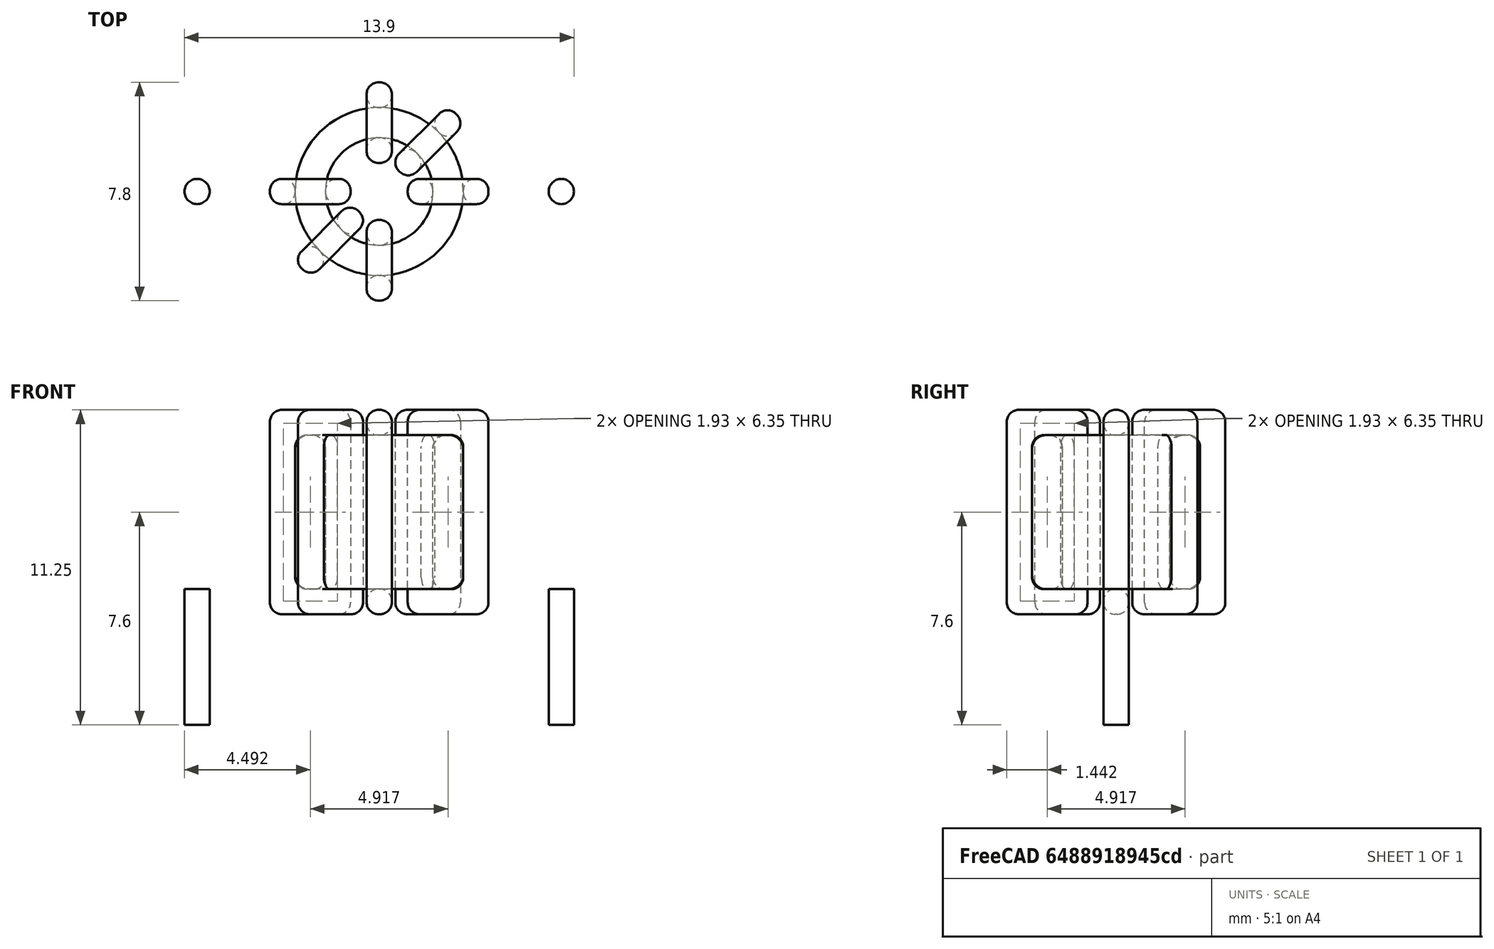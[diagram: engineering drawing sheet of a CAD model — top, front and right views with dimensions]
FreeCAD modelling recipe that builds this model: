
FCSTD DOCUMENT  (FreeCAD 0.16R6703 (Git))
Label: L_Toroid_Horizontal_D7.8mm_P13.00mm_Diameter9-5mm_Amidon-T30
License: All rights reserved
LicenseURL: http://en.wikipedia.org/wiki/All_rights_reserved
objects: Sketcher::SketchObject×6, PartDesign::Pad×6, PartDesign::Fillet×5, Spreadsheet::Sheet×1
note: 23 computed .brp shape members not serialized (recipe doc carries the construction recipe); baked Part::Feature solids carry a one-line shape summary decoded from their .brp

FEATURE [Spreadsheet::Sheet] Spreadsheet  label="dimensions"
  cells = A1=Wx; B1(Wx)=7.7978; C1(WW)=3.8354; D1=7.7978; A2=Wy; B2(Wy)=7.7978; D2=7.7978; A3=RM; B3(RMx)=13; C3(RMy)=0; A4=d_wire; B4(d_wire)=0.8999999999999999; A5=H; B5(H)=5.5; A6=offsetx; B6(offsetx)=-2.6011
FEATURE [Sketcher::SketchObject] Sketch
  Placement = pos=(0,0,1.4) rot=(0,0,1;0rad)
  expr: Placement.Base.z = 0.5 + Spreadsheet.d_wire
  expr: Constraints[0] = Spreadsheet.Wx / 2 - Spreadsheet.d_wire
  expr: Constraints[4] = Spreadsheet.WW / 2
  expr: Constraints[2] = Spreadsheet.RMy / 2
  expr: Constraints[1] = Spreadsheet.RMx / 2
  sketch-geometry (2):
    g0: Circle CenterX=6.5 CenterY=0 CenterZ=0 NormalX=0 NormalY=0 NormalZ=1 Radius=2.9989
    g1: Circle CenterX=6.5 CenterY=0 CenterZ=0 NormalX=0 NormalY=0 NormalZ=1 Radius=1.9177
  constraints (5):
    c: Radius(g0) = 2.9989
    c: DistanceX(g-1,g0) = 6.5
    c: DistanceY(g-1,g0) = 0
    c: Coincident(g1,g0)
    c: Radius(g1) = 1.9177
FEATURE [PartDesign::Pad] Pad
  Length = 5.5
  Length2 = 100
  Placement = pos=(0,0,1.4) rot=(0,0,1;0rad)
  Sketch = -> Sketch
  Type = 0
  expr: Length = Spreadsheet.H
FEATURE [Sketcher::SketchObject] Sketch001
  Placement = pos=(0,0,0.95) rot=(0,0,1;0rad)
  expr: Placement.Base.z = 0.5 + Spreadsheet.d_wire * 0.5
  expr: Constraints[4] = Spreadsheet.RMx
  expr: Constraints[2] = Spreadsheet.RMy
  expr: Constraints[1] = Spreadsheet.d_wire / 2
  sketch-geometry (2):
    g0: Circle CenterX=0 CenterY=0 CenterZ=0 NormalX=0 NormalY=0 NormalZ=1 Radius=0.45
    g1: Circle CenterX=13 CenterY=0 CenterZ=0 NormalX=0 NormalY=0 NormalZ=1 Radius=0.45
  constraints (5):
    c: Equal(g0,g1)
    c: Radius(g0) = 0.45
    c: DistanceY(g-1,g1) = 0
    c: Coincident(g0,g-1)
    c: DistanceX(g-1,g1) = 13
FEATURE [PartDesign::Pad] Pad001
  Length = 0.45
  Length2 = 4.4
  Placement = pos=(0,0,0.95) rot=(0,0,1;0rad)
  Reversed = true
  Sketch = -> Sketch001
  Type = 4
  expr: Length2 = 3.5 + Spreadsheet.d_wire
  expr: Length = Spreadsheet.d_wire / 2
FEATURE [PartDesign::Fillet] Fillet
  Base = -> Pad [Edge6,Edge3,Edge2]
  Placement = pos=(0,0,1.4) rot=(0,0,1;0rad)
  Radius = 0.5
FEATURE [Sketcher::SketchObject] Sketch003
  Placement = pos=(6.5,0,0) rot=(1,0,0;1.5708rad)
  expr: Placement.Base.x = Spreadsheet.RMx / 2
  expr: Constraints[49] = Spreadsheet.Wx - Spreadsheet.d_wire * 2
  expr: Constraints[44] = Spreadsheet.d_wire
  expr: Constraints[23] = Spreadsheet.H
  expr: Constraints[22] = Spreadsheet.Wx / 2 - Spreadsheet.d_wire
  expr: Placement.Base.y = Spreadsheet.RMy / 2
  expr: Constraints[21] = (Spreadsheet.Wx - Spreadsheet.WW) / 2 - Spreadsheet.d_wire
  expr: Constraints[19] = Spreadsheet.d_wire
  expr: Constraints[17] = Spreadsheet.d_wire
  expr: Constraints[18] = Spreadsheet.d_wire
  expr: Constraints[16] = Spreadsheet.d_wire
  sketch-geometry (16):
    g0: LineSegment StartX=-1.0177 StartY=0.5 StartZ=0 EndX=-3.8989 EndY=0.5 EndZ=0
    g1: LineSegment StartX=-3.8989 StartY=0.5 StartZ=0 EndX=-3.8989 EndY=7.8 EndZ=0
    g2: LineSegment StartX=-3.8989 StartY=7.8 StartZ=0 EndX=-1.0177 EndY=7.8 EndZ=0
    g3: LineSegment StartX=-1.0177 StartY=7.8 StartZ=0 EndX=-1.0177 EndY=0.5 EndZ=0
    g4: LineSegment StartX=-2.9989 StartY=6.9 StartZ=0 EndX=-1.9177 EndY=6.9 EndZ=0
    g5: LineSegment StartX=-1.9177 StartY=6.9 StartZ=0 EndX=-1.9177 EndY=1.4 EndZ=0
    g6: LineSegment StartX=-1.9177 StartY=1.4 StartZ=0 EndX=-2.9989 EndY=1.4 EndZ=0
    g7: LineSegment StartX=-2.9989 StartY=1.4 StartZ=0 EndX=-2.9989 EndY=6.9 EndZ=0
    g8: LineSegment StartX=1.0177 StartY=7.8 StartZ=0 EndX=3.8989 EndY=7.8 EndZ=0
    g9: LineSegment StartX=3.8989 StartY=7.8 StartZ=0 EndX=3.8989 EndY=0.5 EndZ=0
    g10: LineSegment StartX=3.8989 StartY=0.5 StartZ=0 EndX=1.0177 EndY=0.5 EndZ=0
    g11: LineSegment StartX=1.0177 StartY=0.5 StartZ=0 EndX=1.0177 EndY=7.8 EndZ=0
    g12: LineSegment StartX=1.9177 StartY=6.9 StartZ=0 EndX=2.9989 EndY=6.9 EndZ=0
    g13: LineSegment StartX=2.9989 StartY=6.9 StartZ=0 EndX=2.9989 EndY=1.4 EndZ=0
    g14: LineSegment StartX=2.9989 StartY=1.4 StartZ=0 EndX=1.9177 EndY=1.4 EndZ=0
    g15: LineSegment StartX=1.9177 StartY=1.4 StartZ=0 EndX=1.9177 EndY=6.9 EndZ=0
  constraints (50):
    c: Horizontal(g0)
    c: Coincident(g1,g0)
    c: Vertical(g1)
    c: Coincident(g2,g1)
    c: Horizontal(g2)
    c: Coincident(g3,g2)
    c: Coincident(g3,g0)
    c: Vertical(g3)
    c: Coincident(g4,g5)
    c: Coincident(g5,g6)
    c: Coincident(g6,g7)
    c: Coincident(g7,g4)
    c: Horizontal(g4)
    c: Horizontal(g6)
    c: Vertical(g5)
    c: Vertical(g7)
    c: DistanceX(g1,g4) = 0.9
    c: DistanceY(g4,g1) = 0.9
    c: DistanceX(g5,g0) = 0.9
    c: DistanceY(g0,g5) = 0.9
    c: DistanceY(g-1,g0) = 0.5
    c: DistanceX(g6,g6) = 1.0812
    c: DistanceX(g6,g-1) = 2.9989
    c: DistanceY(g7,g7) = 5.5
    c: Coincident(g8,g9)
    c: Coincident(g9,g10)
    c: Coincident(g10,g11)
    c: Coincident(g11,g8)
    c: Horizontal(g8)
    c: Horizontal(g10)
    c: Vertical(g9)
    c: Vertical(g11)
    c: Coincident(g12,g13)
    c: Coincident(g13,g14)
    c: Coincident(g14,g15)
    c: Coincident(g15,g12)
    c: Horizontal(g12)
    c: Horizontal(g14)
    c: Vertical(g13)
    c: Vertical(g15)
    c: DistanceY(g8,g2) = 0
    c: DistanceY(g10,g0) = 0
    c: DistanceY(g14,g5) = 0
    c: DistanceY(g12,g4) = 0
    c: DistanceX(g8,g12) = 0.9
    c: Equal(g8,g2)
    c: Equal(g12,g4)
    c: Equal(g9,g1)
    c: Equal(g13,g7)
    c: DistanceX(g4,g12) = 5.9978
FEATURE [PartDesign::Pad] Pad002
  Length = 0.9
  Length2 = 100
  Midplane = true
  Placement = pos=(6.5,0,0) rot=(1,0,0;1.5708rad)
  Sketch = -> Sketch003
  Type = 0
  expr: Length = Spreadsheet.d_wire
FEATURE [PartDesign::Fillet] Fillet001
  Base = -> Pad002 [Edge38,Edge41,Edge42,Edge43,Edge29,Edge32,Edge33,Edge34,Edge25,Edge35,Edge36,Edge13,Edge14,Edge15,Edge16,Edge17,Edge18,Edge19,Edge1,Edge2,Edge3,Edge4,Edge5,Edge6,Edge7,Edge37,Edge39,Edge40,Edge20,Edge23,Edge24,Edge21,Edge22,Edge8,Edge9,Edge10,Edge11,Edge12,Edge26,Edge27,+8 more]
  Placement = pos=(6.5,0,0) rot=(1,0,0;1.5708rad)
  Radius = 0.423
  expr: Radius = Spreadsheet.d_wire * 0.47
FEATURE [Sketcher::SketchObject] Sketch004
  Placement = pos=(6.5,0,0) rot=(0.862856,0.357407,0.357407;1.71777rad)
  expr: Placement.Base.x = Spreadsheet.RMx / 2
  expr: Constraints[49] = Spreadsheet.Wx - 2 * Spreadsheet.d_wire
  expr: Constraints[44] = Spreadsheet.d_wire
  expr: Constraints[23] = Spreadsheet.H
  expr: Constraints[22] = Spreadsheet.Wx / 2 - Spreadsheet.d_wire
  expr: Placement.Base.y = Spreadsheet.RMy / 2
  expr: Constraints[21] = (Spreadsheet.Wx - Spreadsheet.WW) / 2 - Spreadsheet.d_wire
  expr: Constraints[19] = Spreadsheet.d_wire
  expr: Constraints[17] = Spreadsheet.d_wire
  expr: Constraints[18] = Spreadsheet.d_wire
  expr: Constraints[16] = Spreadsheet.d_wire
  sketch-geometry (16):
    g0: LineSegment StartX=-1.0177 StartY=0.5 StartZ=0 EndX=-3.8989 EndY=0.5 EndZ=0
    g1: LineSegment StartX=-3.8989 StartY=0.5 StartZ=0 EndX=-3.8989 EndY=7.8 EndZ=0
    g2: LineSegment StartX=-3.8989 StartY=7.8 StartZ=0 EndX=-1.0177 EndY=7.8 EndZ=0
    g3: LineSegment StartX=-1.0177 StartY=7.8 StartZ=0 EndX=-1.0177 EndY=0.5 EndZ=0
    g4: LineSegment StartX=-2.9989 StartY=6.9 StartZ=0 EndX=-1.9177 EndY=6.9 EndZ=0
    g5: LineSegment StartX=-1.9177 StartY=6.9 StartZ=0 EndX=-1.9177 EndY=1.4 EndZ=0
    g6: LineSegment StartX=-1.9177 StartY=1.4 StartZ=0 EndX=-2.9989 EndY=1.4 EndZ=0
    g7: LineSegment StartX=-2.9989 StartY=1.4 StartZ=0 EndX=-2.9989 EndY=6.9 EndZ=0
    g8: LineSegment StartX=1.0177 StartY=7.8 StartZ=0 EndX=3.8989 EndY=7.8 EndZ=0
    g9: LineSegment StartX=3.8989 StartY=7.8 StartZ=0 EndX=3.8989 EndY=0.5 EndZ=0
    g10: LineSegment StartX=3.8989 StartY=0.5 StartZ=0 EndX=1.0177 EndY=0.5 EndZ=0
    g11: LineSegment StartX=1.0177 StartY=0.5 StartZ=0 EndX=1.0177 EndY=7.8 EndZ=0
    g12: LineSegment StartX=1.9177 StartY=6.9 StartZ=0 EndX=2.9989 EndY=6.9 EndZ=0
    g13: LineSegment StartX=2.9989 StartY=6.9 StartZ=0 EndX=2.9989 EndY=1.4 EndZ=0
    g14: LineSegment StartX=2.9989 StartY=1.4 StartZ=0 EndX=1.9177 EndY=1.4 EndZ=0
    g15: LineSegment StartX=1.9177 StartY=1.4 StartZ=0 EndX=1.9177 EndY=6.9 EndZ=0
  constraints (50):
    c: Horizontal(g0)
    c: Coincident(g1,g0)
    c: Vertical(g1)
    c: Coincident(g2,g1)
    c: Horizontal(g2)
    c: Coincident(g3,g2)
    c: Coincident(g3,g0)
    c: Vertical(g3)
    c: Coincident(g4,g5)
    c: Coincident(g5,g6)
    c: Coincident(g6,g7)
    c: Coincident(g7,g4)
    c: Horizontal(g4)
    c: Horizontal(g6)
    c: Vertical(g5)
    c: Vertical(g7)
    c: DistanceX(g1,g4) = 0.9
    c: DistanceY(g4,g1) = 0.9
    c: DistanceX(g5,g0) = 0.9
    c: DistanceY(g0,g5) = 0.9
    c: DistanceY(g-1,g0) = 0.5
    c: DistanceX(g6,g6) = 1.0812
    c: DistanceX(g6,g-1) = 2.9989
    c: DistanceY(g7,g7) = 5.5
    c: Coincident(g8,g9)
    c: Coincident(g9,g10)
    c: Coincident(g10,g11)
    c: Coincident(g11,g8)
    c: Horizontal(g8)
    c: Horizontal(g10)
    c: Vertical(g9)
    c: Vertical(g11)
    c: Coincident(g12,g13)
    c: Coincident(g13,g14)
    c: Coincident(g14,g15)
    c: Coincident(g15,g12)
    c: Horizontal(g12)
    c: Horizontal(g14)
    c: Vertical(g13)
    c: Vertical(g15)
    c: DistanceY(g8,g2) = 0
    c: DistanceY(g10,g0) = 0
    c: DistanceY(g14,g5) = 0
    c: DistanceY(g12,g4) = 0
    c: DistanceX(g8,g12) = 0.9
    c: Equal(g8,g2)
    c: Equal(g12,g4)
    c: Equal(g9,g1)
    c: Equal(g13,g7)
    c: DistanceX(g4,g12) = 5.9978
FEATURE [PartDesign::Pad] Pad003
  Length = 0.9
  Length2 = 100
  Midplane = true
  Placement = pos=(6.5,0,0) rot=(0.862856,0.357407,0.357407;1.71777rad)
  Sketch = -> Sketch004
  Type = 0
  expr: Length = Spreadsheet.d_wire
FEATURE [PartDesign::Fillet] Fillet002
  Base = -> Pad003 [Edge38,Edge41,Edge42,Edge43,Edge29,Edge32,Edge33,Edge34,Edge25,Edge35,Edge36,Edge13,Edge14,Edge15,Edge16,Edge17,Edge18,Edge19,Edge1,Edge2,Edge3,Edge4,Edge5,Edge6,Edge7,Edge37,Edge39,Edge40,Edge20,Edge23,Edge24,Edge21,Edge22,Edge8,Edge9,Edge10,Edge11,Edge12,Edge26,Edge27,+8 more]
  Placement = pos=(6.5,0,0) rot=(0.862856,0.357407,0.357407;1.71777rad)
  Radius = 0.423
  expr: Radius = Spreadsheet.d_wire * 0.47
FEATURE [Sketcher::SketchObject] Sketch005
  Placement = pos=(6.5,0,0) rot=(0.862856,-0.357407,-0.357407;1.71777rad)
  expr: Placement.Base.x = Spreadsheet.RMx / 2
  expr: Constraints[49] = Spreadsheet.Wx - 2 * Spreadsheet.d_wire
  expr: Constraints[44] = Spreadsheet.d_wire
  expr: Constraints[23] = Spreadsheet.H
  expr: Constraints[22] = Spreadsheet.Wx / 2 - Spreadsheet.d_wire
  expr: Placement.Base.y = Spreadsheet.RMy / 2
  expr: Constraints[21] = (Spreadsheet.Wx - Spreadsheet.WW) / 2 - Spreadsheet.d_wire
  expr: Constraints[19] = Spreadsheet.d_wire
  expr: Constraints[17] = Spreadsheet.d_wire
  expr: Constraints[18] = Spreadsheet.d_wire
  expr: Constraints[16] = Spreadsheet.d_wire
  sketch-geometry (16):
    g0: LineSegment StartX=-1.0177 StartY=0.5 StartZ=0 EndX=-3.8989 EndY=0.5 EndZ=0
    g1: LineSegment StartX=-3.8989 StartY=0.5 StartZ=0 EndX=-3.8989 EndY=7.8 EndZ=0
    g2: LineSegment StartX=-3.8989 StartY=7.8 StartZ=0 EndX=-1.0177 EndY=7.8 EndZ=0
    g3: LineSegment StartX=-1.0177 StartY=7.8 StartZ=0 EndX=-1.0177 EndY=0.5 EndZ=0
    g4: LineSegment StartX=-2.9989 StartY=6.9 StartZ=0 EndX=-1.9177 EndY=6.9 EndZ=0
    g5: LineSegment StartX=-1.9177 StartY=6.9 StartZ=0 EndX=-1.9177 EndY=1.4 EndZ=0
    g6: LineSegment StartX=-1.9177 StartY=1.4 StartZ=0 EndX=-2.9989 EndY=1.4 EndZ=0
    g7: LineSegment StartX=-2.9989 StartY=1.4 StartZ=0 EndX=-2.9989 EndY=6.9 EndZ=0
    g8: LineSegment StartX=1.0177 StartY=7.8 StartZ=0 EndX=3.8989 EndY=7.8 EndZ=0
    g9: LineSegment StartX=3.8989 StartY=7.8 StartZ=0 EndX=3.8989 EndY=0.5 EndZ=0
    g10: LineSegment StartX=3.8989 StartY=0.5 StartZ=0 EndX=1.0177 EndY=0.5 EndZ=0
    g11: LineSegment StartX=1.0177 StartY=0.5 StartZ=0 EndX=1.0177 EndY=7.8 EndZ=0
    g12: LineSegment StartX=1.9177 StartY=6.9 StartZ=0 EndX=2.9989 EndY=6.9 EndZ=0
    g13: LineSegment StartX=2.9989 StartY=6.9 StartZ=0 EndX=2.9989 EndY=1.4 EndZ=0
    g14: LineSegment StartX=2.9989 StartY=1.4 StartZ=0 EndX=1.9177 EndY=1.4 EndZ=0
    g15: LineSegment StartX=1.9177 StartY=1.4 StartZ=0 EndX=1.9177 EndY=6.9 EndZ=0
  constraints (50):
    c: Horizontal(g0)
    c: Coincident(g1,g0)
    c: Vertical(g1)
    c: Coincident(g2,g1)
    c: Horizontal(g2)
    c: Coincident(g3,g2)
    c: Coincident(g3,g0)
    c: Vertical(g3)
    c: Coincident(g4,g5)
    c: Coincident(g5,g6)
    c: Coincident(g6,g7)
    c: Coincident(g7,g4)
    c: Horizontal(g4)
    c: Horizontal(g6)
    c: Vertical(g5)
    c: Vertical(g7)
    c: DistanceX(g1,g4) = 0.9
    c: DistanceY(g4,g1) = 0.9
    c: DistanceX(g5,g0) = 0.9
    c: DistanceY(g0,g5) = 0.9
    c: DistanceY(g-1,g0) = 0.5
    c: DistanceX(g6,g6) = 1.0812
    c: DistanceX(g6,g-1) = 2.9989
    c: DistanceY(g7,g7) = 5.5
    c: Coincident(g8,g9)
    c: Coincident(g9,g10)
    c: Coincident(g10,g11)
    c: Coincident(g11,g8)
    c: Horizontal(g8)
    c: Horizontal(g10)
    c: Vertical(g9)
    c: Vertical(g11)
    c: Coincident(g12,g13)
    c: Coincident(g13,g14)
    c: Coincident(g14,g15)
    c: Coincident(g15,g12)
    c: Horizontal(g12)
    c: Horizontal(g14)
    c: Vertical(g13)
    c: Vertical(g15)
    c: DistanceY(g8,g2) = 0
    c: DistanceY(g10,g0) = 0
    c: DistanceY(g14,g5) = 0
    c: DistanceY(g12,g4) = 0
    c: DistanceX(g8,g12) = 0.9
    c: Equal(g8,g2)
    c: Equal(g12,g4)
    c: Equal(g9,g1)
    c: Equal(g13,g7)
    c: DistanceX(g4,g12) = 5.9978
FEATURE [PartDesign::Pad] Pad004
  Length = 0.9
  Length2 = 100
  Midplane = true
  Placement = pos=(6.5,0,0) rot=(0.862856,-0.357407,-0.357407;1.71777rad)
  Sketch = -> Sketch005
  Type = 0
  expr: Length = Spreadsheet.d_wire
FEATURE [PartDesign::Fillet] Fillet003
  Base = -> Pad004 [Edge38,Edge41,Edge42,Edge43,Edge29,Edge32,Edge33,Edge34,Edge25,Edge35,Edge36,Edge13,Edge14,Edge15,Edge16,Edge17,Edge18,Edge19,Edge1,Edge2,Edge3,Edge4,Edge5,Edge6,Edge7,Edge37,Edge39,Edge40,Edge20,Edge23,Edge24,Edge21,Edge22,Edge8,Edge9,Edge10,Edge11,Edge12,Edge26,Edge27,+8 more]
  Placement = pos=(6.5,0,0) rot=(0.862856,-0.357407,-0.357407;1.71777rad)
  Radius = 0.423
  expr: Radius = Spreadsheet.d_wire * 0.47
FEATURE [Sketcher::SketchObject] Sketch006
  Placement = pos=(6.5,0,0) rot=(0.57735,0.57735,0.57735;2.0944rad)
  expr: Placement.Base.x = Spreadsheet.RMx / 2
  expr: Constraints[49] = Spreadsheet.Wx - Spreadsheet.d_wire * 2
  expr: Constraints[44] = Spreadsheet.d_wire
  expr: Constraints[23] = Spreadsheet.H
  expr: Constraints[22] = Spreadsheet.Wx / 2 - Spreadsheet.d_wire
  expr: Placement.Base.y = Spreadsheet.RMy / 2
  expr: Constraints[21] = (Spreadsheet.Wx - Spreadsheet.WW) / 2 - Spreadsheet.d_wire
  expr: Constraints[19] = Spreadsheet.d_wire
  expr: Constraints[17] = Spreadsheet.d_wire
  expr: Constraints[18] = Spreadsheet.d_wire
  expr: Constraints[16] = Spreadsheet.d_wire
  sketch-geometry (16):
    g0: LineSegment StartX=-1.0177 StartY=0.5 StartZ=0 EndX=-3.8989 EndY=0.5 EndZ=0
    g1: LineSegment StartX=-3.8989 StartY=0.5 StartZ=0 EndX=-3.8989 EndY=7.8 EndZ=0
    g2: LineSegment StartX=-3.8989 StartY=7.8 StartZ=0 EndX=-1.0177 EndY=7.8 EndZ=0
    g3: LineSegment StartX=-1.0177 StartY=7.8 StartZ=0 EndX=-1.0177 EndY=0.5 EndZ=0
    g4: LineSegment StartX=-2.9989 StartY=6.9 StartZ=0 EndX=-1.9177 EndY=6.9 EndZ=0
    g5: LineSegment StartX=-1.9177 StartY=6.9 StartZ=0 EndX=-1.9177 EndY=1.4 EndZ=0
    g6: LineSegment StartX=-1.9177 StartY=1.4 StartZ=0 EndX=-2.9989 EndY=1.4 EndZ=0
    g7: LineSegment StartX=-2.9989 StartY=1.4 StartZ=0 EndX=-2.9989 EndY=6.9 EndZ=0
    g8: LineSegment StartX=1.0177 StartY=7.8 StartZ=0 EndX=3.8989 EndY=7.8 EndZ=0
    g9: LineSegment StartX=3.8989 StartY=7.8 StartZ=0 EndX=3.8989 EndY=0.5 EndZ=0
    g10: LineSegment StartX=3.8989 StartY=0.5 StartZ=0 EndX=1.0177 EndY=0.5 EndZ=0
    g11: LineSegment StartX=1.0177 StartY=0.5 StartZ=0 EndX=1.0177 EndY=7.8 EndZ=0
    g12: LineSegment StartX=1.9177 StartY=6.9 StartZ=0 EndX=2.9989 EndY=6.9 EndZ=0
    g13: LineSegment StartX=2.9989 StartY=6.9 StartZ=0 EndX=2.9989 EndY=1.4 EndZ=0
    g14: LineSegment StartX=2.9989 StartY=1.4 StartZ=0 EndX=1.9177 EndY=1.4 EndZ=0
    g15: LineSegment StartX=1.9177 StartY=1.4 StartZ=0 EndX=1.9177 EndY=6.9 EndZ=0
  constraints (50):
    c: Horizontal(g0)
    c: Coincident(g1,g0)
    c: Vertical(g1)
    c: Coincident(g2,g1)
    c: Horizontal(g2)
    c: Coincident(g3,g2)
    c: Coincident(g3,g0)
    c: Vertical(g3)
    c: Coincident(g4,g5)
    c: Coincident(g5,g6)
    c: Coincident(g6,g7)
    c: Coincident(g7,g4)
    c: Horizontal(g4)
    c: Horizontal(g6)
    c: Vertical(g5)
    c: Vertical(g7)
    c: DistanceX(g1,g4) = 0.9
    c: DistanceY(g4,g1) = 0.9
    c: DistanceX(g5,g0) = 0.9
    c: DistanceY(g0,g5) = 0.9
    c: DistanceY(g-1,g0) = 0.5
    c: DistanceX(g6,g6) = 1.0812
    c: DistanceX(g6,g-1) = 2.9989
    c: DistanceY(g7,g7) = 5.5
    c: Coincident(g8,g9)
    c: Coincident(g9,g10)
    c: Coincident(g10,g11)
    c: Coincident(g11,g8)
    c: Horizontal(g8)
    c: Horizontal(g10)
    c: Vertical(g9)
    c: Vertical(g11)
    c: Coincident(g12,g13)
    c: Coincident(g13,g14)
    c: Coincident(g14,g15)
    c: Coincident(g15,g12)
    c: Horizontal(g12)
    c: Horizontal(g14)
    c: Vertical(g13)
    c: Vertical(g15)
    c: DistanceY(g8,g2) = 0
    c: DistanceY(g10,g0) = 0
    c: DistanceY(g14,g5) = 0
    c: DistanceY(g12,g4) = 0
    c: DistanceX(g8,g12) = 0.9
    c: Equal(g8,g2)
    c: Equal(g12,g4)
    c: Equal(g9,g1)
    c: Equal(g13,g7)
    c: DistanceX(g4,g12) = 5.9978
FEATURE [PartDesign::Pad] Pad005
  Length = 0.9
  Length2 = 100
  Midplane = true
  Placement = pos=(6.5,0,0) rot=(0.57735,0.57735,0.57735;2.0944rad)
  Sketch = -> Sketch006
  Type = 0
  expr: Length = Spreadsheet.d_wire
FEATURE [PartDesign::Fillet] Fillet004
  Base = -> Pad005 [Edge38,Edge41,Edge42,Edge43,Edge29,Edge32,Edge33,Edge34,Edge25,Edge35,Edge36,Edge13,Edge14,Edge15,Edge16,Edge17,Edge18,Edge19,Edge1,Edge2,Edge3,Edge4,Edge5,Edge6,Edge7,Edge37,Edge39,Edge40,Edge20,Edge23,Edge24,Edge21,Edge22,Edge8,Edge9,Edge10,Edge11,Edge12,Edge26,Edge27,+8 more]
  Placement = pos=(6.5,0,0) rot=(0.57735,0.57735,0.57735;2.0944rad)
  Radius = 0.423
  expr: Radius = Spreadsheet.d_wire * 0.47
